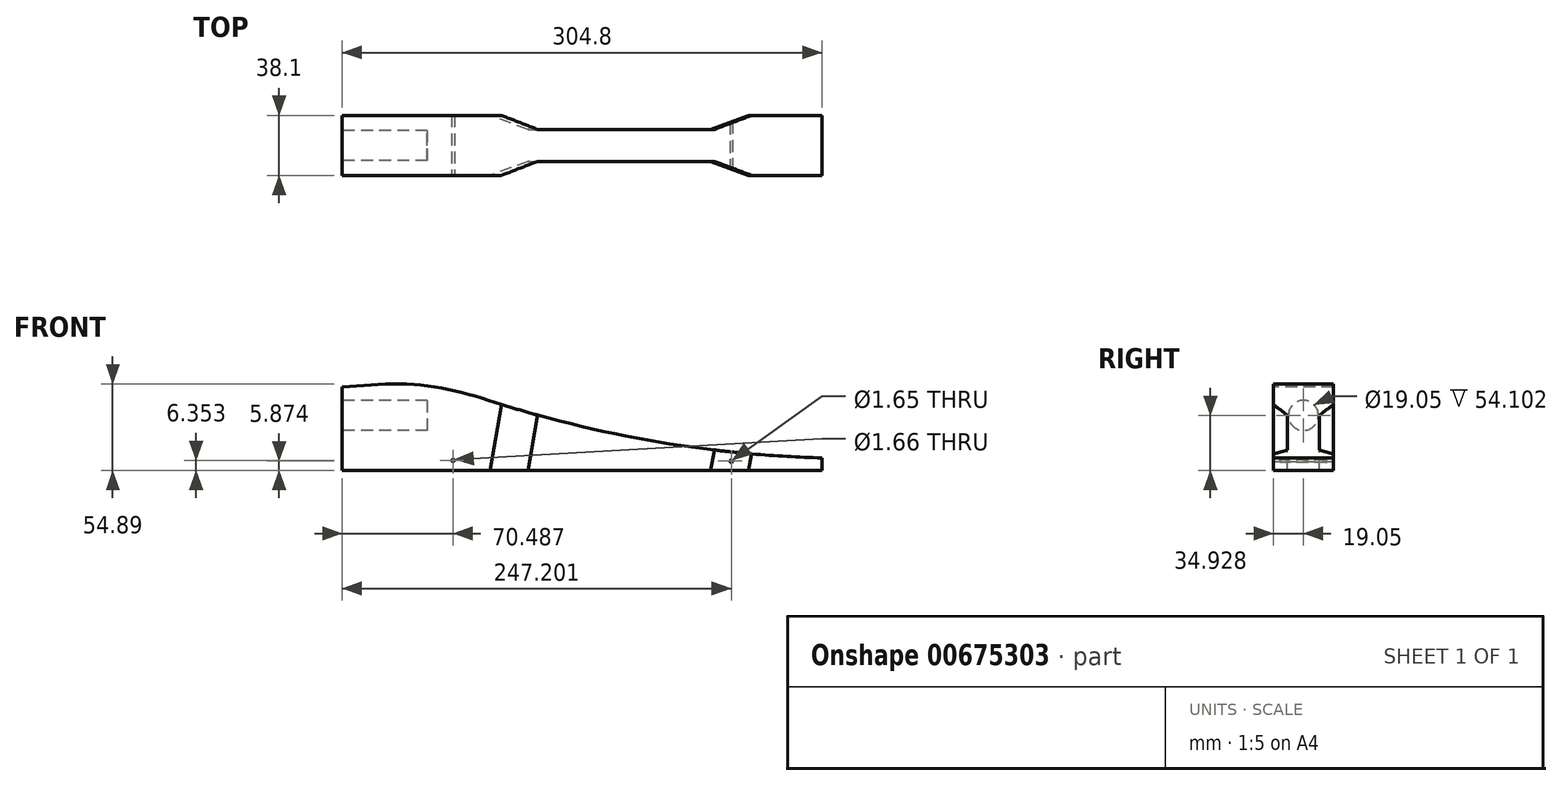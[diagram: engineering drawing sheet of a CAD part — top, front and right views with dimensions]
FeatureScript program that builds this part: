
annotation { "Feature Type Name" : "Feature", "Feature Type Description" : "" }
export const myFeature = defineFeature(function(context is Context, id is Id, definition is map)
    precondition{}
    {
        {
            var Q0;
            Q0=qCreatedBy(makeId("Front.planeOp"),FACE);
            var sketch = newSketch(context, id + "F0", { "sketchPlane" : qUnion([Q0])});
            skLineSegment(sketch, "E0.bottom", {"start": v(-104.5, 9.8) * mm, "end": v(200.3, 9.8) * mm});
            skLineSegment(sketch, "E0.top", {"start": v(-104.5, -60.06) * mm, "end": v(200.3, -60.06) * mm});
            skLineSegment(sketch, "E0.left", {"start": v(-104.5, 9.8) * mm, "end": v(-104.5, -60.06) * mm});
            skLineSegment(sketch, "E0.right", {"start": v(200.3, 9.8) * mm, "end": v(200.3, -60.06) * mm});
            skSolve(sketch);
        }
        {
            var Q0;
            Q0=makeQuery(id+"F0.imprint","IMPRINT",FACE,{"disambiguationData":[TD([[makeQuery(id+"F0.imprint","IMPRINT",EDGE,{"derivedFrom":sQuery(id+"F0.wireOp",EDGE,"E0.bottom")}),-1.0]])]});
            extrude(context, id + "F1", {"entities" : qUnion([Q0]), "oppositeDirection" : true, "depth" : 38.1 * mm, "offsetDistance" : 25.4 * mm});
        }
        {
            var Q0;
            Q0=makeQuery(id+"F1.opExtrude","CAP_FACE",FACE,{"disambiguationData":[OSD([sQuery(id+"F0.wireOp",EDGE,"E0.bottom"),sQuery(id+"F0.wireOp",EDGE,"E0.top"),sQuery(id+"F0.wireOp",EDGE,"E0.left"),sQuery(id+"F0.wireOp",EDGE,"E0.right")])],"isStart":true});
            var sketch = newSketch(context, id + "F2", { "sketchPlane" : qUnion([Q0])});
            skLineSegment(sketch, "E1", {"start": v(-104.5, 9.8) * mm, "end": v(200.3, -44.18) * mm});
            skLineSegment(sketch, "E2", {"start": v(200.3, -44.18) * mm, "end": v(200.3, -60.06) * mm});
            skLineSegment(sketch, "E3", {"start": v(200.3, -60.06) * mm, "end": v(-104.5, -60.06) * mm});
            skLineSegment(sketch, "E4", {"start": v(-104.5, -60.06) * mm, "end": v(-104.5, 9.8) * mm});
            skSolve(sketch);
        }
        {
            var Q0;
            {var subQ0=sQuery(id+"F2.wireOp",EDGE,"E1");Q0=makeQuery(id+"F2.imprint","IMPRINT",FACE,{"disambiguationData":[TD([[makeQuery(id+"F2.imprint","IMPRINT",EDGE,{"derivedFrom":subQ0}),1.0]])]});}
            extrude(context, id + "F3", {"entities" : qUnion([Q0]), "operationType" : NewBodyOperationType.REMOVE, "oppositeDirection" : true, "depth" : 50.8 * mm, "offsetDistance" : 25.4 * mm});
        }
        {
            var Q0;
            Q0=makeQuery(id+"F1.opExtrude","SWEPT_FACE",FACE,{"disambiguationData":[OSD([sQuery(id+"F0.wireOp",EDGE,"E0.left")])]});
            var sketch = newSketch(context, id + "F4", { "sketchPlane" : qUnion([Q0])});
            skCircle(sketch, "E5", {"center": v(-19.05, -25.13) * mm, "radius": 9.53 * mm});
            skPoint(sketch, "E6.orphan", {"position": v(-19.05, 9.8) * mm});
            skPoint(sketch, "E7.start.orphan", {"position": v(-38.1, -25.13) * mm});
            skPoint(sketch, "E8.trimOffspring.end.orphan", {"position": v(0, -25.13) * mm});
            skPoint(sketch, "E9.end.orphan", {"position": v(-19.05, -60.06) * mm});
            skSolve(sketch);
        }
        {
            var Q0;
            Q0=makeQuery(id+"F4.imprint","IMPRINT",FACE,{"disambiguationData":[TD([[makeQuery(id+"F4.imprint","IMPRINT",EDGE,{"derivedFrom":sQuery(id+"F4.wireOp",EDGE,"E5")}),1.0]])]});
            extrude(context, id + "F5", {"entities" : qUnion([Q0]), "operationType" : NewBodyOperationType.REMOVE, "oppositeDirection" : true, "depth" : 54.1 * mm, "offsetDistance" : 25.4 * mm});
        }
        {
            var Q0;
            Q0=makeQuery(id+"F3.boolean.opBoolean","COPY",FACE,{"derivedFrom":makeQuery(id+"F3.opExtrude","SWEPT_FACE",FACE,{"disambiguationData":[OSD([sQuery(id+"F2.wireOp",EDGE,"E1")])]})});
            var sketch = newSketch(context, id + "F6", { "sketchPlane" : qUnion([Q0])});
            skLineSegment(sketch, "E10", {"start": v(0, 0) * mm, "end": v(23.78, 8.92) * mm});
            skLineSegment(sketch, "E11", {"start": v(23.78, 8.92) * mm, "end": v(138.08, 8.92) * mm});
            skLineSegment(sketch, "E12", {"start": v(138.08, 8.92) * mm, "end": v(161.86, 0) * mm});
            skLineSegment(sketch, "E13", {"start": v(161.86, 0) * mm, "end": v(0, 0) * mm});
            skPoint(sketch, "E14.MirrorCS.end.orphan", {"position": v(109.86, 84.13) * mm});
            skPoint(sketch, "E14.MirrorCS.start.orphan", {"position": v(23.78, 8.92) * mm});
            skLineSegment(sketch, "E15", {"start": v(0, 38.1) * mm, "end": v(23.78, 29.18) * mm});
            skLineSegment(sketch, "E16", {"start": v(23.78, 29.18) * mm, "end": v(138.08, 29.18) * mm});
            skLineSegment(sketch, "E17", {"start": v(138.08, 29.18) * mm, "end": v(161.86, 38.1) * mm});
            skLineSegment(sketch, "E18", {"start": v(161.86, 38.1) * mm, "end": v(0, 38.1) * mm});
            skSolve(sketch);
        }
        {
            var Q0;
            Q0=makeQuery(id+"F6.imprint","IMPRINT",FACE,{"disambiguationData":[TD([[makeQuery(id+"F6.imprint","IMPRINT",EDGE,{"derivedFrom":sQuery(id+"F6.wireOp",EDGE,"E15")}),1.0]])]});
            var Q1;
            Q1=makeQuery(id+"F6.imprint","IMPRINT",FACE,{"disambiguationData":[TD([[makeQuery(id+"F6.imprint","IMPRINT",EDGE,{"derivedFrom":sQuery(id+"F6.wireOp",EDGE,"E10")}),-1.0]])]});
            extrude(context, id + "F7", {"entities" : qUnion([Q0, Q1]), "operationType" : NewBodyOperationType.REMOVE, "oppositeDirection" : true, "depth" : 127 * mm, "offsetDistance" : 25.4 * mm});
        }
        {
            var Q0;
            {var subQ0=sQuery(id+"F0.wireOp",EDGE,"E0.top");var subQ1=sQuery(id+"F0.wireOp",EDGE,"E0.left");Q0=makeQuery(id+"F7.boolean.opBoolean","SPLIT",FACE,{"disambiguationData":[TD([makeQuery(id+"F1.opExtrude","SWEPT_FACE",FACE,{"disambiguationData":[OSD([subQ1])]})])],"derivedFrom":makeQuery(id+"F1.opExtrude","CAP_FACE",FACE,{"disambiguationData":[OSD([sQuery(id+"F0.wireOp",EDGE,"E0.bottom"),subQ0,subQ1,sQuery(id+"F0.wireOp",EDGE,"E0.right")])],"isStart":true})});}
            var sketch = newSketch(context, id + "F8", { "sketchPlane" : qUnion([Q0])});
            skFitSpline(sketch, "E19", {"points": [v(-104.5, -7.03) * mm, v(-51.46, -6.13) * mm, v(-3.22, -18.16) * mm], "startDerivative": vector(105.99, 8.43) * mm, "endDerivative": vector(96.51, -30.92) * mm});
            skSolve(sketch);
        }
        {
            var Q0;
            Q0=qCreatedBy(makeId("Front.planeOp"),FACE);
            var sketch = newSketch(context, id + "F9", { "sketchPlane" : qUnion([Q0])});
            skLineSegment(sketch, "E20.0.0", {"start": v(13.52, -60.06) * mm, "end": v(21.92, -12.6) * mm});
            skLineSegment(sketch, "E20.0.1", {"start": v(21.92, -12.6) * mm, "end": v(-1.5, -8.45) * mm});
            skLineSegment(sketch, "E20.0.2", {"start": v(-1.5, -8.45) * mm, "end": v(-3.22, -18.16) * mm});
            skLineSegment(sketch, "E20.0.3", {"start": v(-3.22, -18.16) * mm, "end": v(-10.64, -60.06) * mm});
            skLineSegment(sketch, "E20.0.4", {"start": v(-10.64, -60.06) * mm, "end": v(13.52, -60.06) * mm});
            skLineSegment(sketch, "E21.0.0", {"start": v(129.6, -60.06) * mm, "end": v(134.47, -32.52) * mm});
            skLineSegment(sketch, "E21.0.1", {"start": v(134.47, -32.52) * mm, "end": v(21.92, -12.6) * mm});
            skLineSegment(sketch, "E21.0.2", {"start": v(21.92, -12.6) * mm, "end": v(13.52, -60.06) * mm});
            skLineSegment(sketch, "E21.0.3", {"start": v(13.52, -60.06) * mm, "end": v(129.6, -60.06) * mm});
            skLineSegment(sketch, "E22.0.0", {"start": v(153.74, -60.06) * mm, "end": v(157.89, -36.67) * mm});
            skLineSegment(sketch, "E22.0.1", {"start": v(157.89, -36.67) * mm, "end": v(134.47, -32.52) * mm});
            skLineSegment(sketch, "E22.0.2", {"start": v(134.47, -32.52) * mm, "end": v(129.6, -60.06) * mm});
            skLineSegment(sketch, "E22.0.3", {"start": v(129.6, -60.06) * mm, "end": v(153.74, -60.06) * mm});
            skLineSegment(sketch, "E23.0.0", {"start": v(157.89, -36.67) * mm, "end": v(153.74, -60.06) * mm});
            skLineSegment(sketch, "E23.0.1", {"start": v(153.74, -60.06) * mm, "end": v(200.3, -60.06) * mm});
            skLineSegment(sketch, "E23.0.2", {"start": v(200.3, -60.06) * mm, "end": v(200.3, -44.18) * mm});
            skLineSegment(sketch, "E23.0.3", {"start": v(200.3, -44.18) * mm, "end": v(157.89, -36.67) * mm});
            skArc(sketch, "E24", {"start": v(-3.22, -18.16) * mm, "mid": v(97.38, -42.15) * mm, "end": v(200.3, -52.12) * mm});
            skSolve(sketch);
        }
        {
            var Q0;
            {var subQ0=sQuery(id+"F8.wireOp",EDGE,"E19");Q0=makeQuery(id+"F8.imprint","IMPRINT",FACE,{"disambiguationData":[TD([[makeQuery(id+"F8.imprint","IMPRINT",EDGE,{"derivedFrom":subQ0}),1.0]])]});}
            var Q1;
            {var subQ0=sQuery(id+"F9.wireOp",EDGE,"E20.0.1");Q1=makeQuery(id+"F9.imprint","IMPRINT",FACE,{"disambiguationData":[TD([[makeQuery(id+"F9.imprint","IMPRINT",EDGE,{"derivedFrom":subQ0}),1.0]])]});}
            var Q2;
            {var subQ0=sQuery(id+"F9.wireOp",EDGE,"E23.0.3");Q2=makeQuery(id+"F9.imprint","IMPRINT",FACE,{"disambiguationData":[TD([[makeQuery(id+"F9.imprint","IMPRINT",EDGE,{"derivedFrom":subQ0}),1.0]])]});}
            var Q3;
            {var subQ0=sQuery(id+"F9.wireOp",EDGE,"E22.0.1");Q3=makeQuery(id+"F9.imprint","IMPRINT",FACE,{"disambiguationData":[TD([[makeQuery(id+"F9.imprint","IMPRINT",EDGE,{"derivedFrom":subQ0}),1.0]])]});}
            var Q4;
            {var subQ0=sQuery(id+"F9.wireOp",EDGE,"E21.0.1");Q4=makeQuery(id+"F9.imprint","IMPRINT",FACE,{"disambiguationData":[TD([[makeQuery(id+"F9.imprint","IMPRINT",EDGE,{"derivedFrom":subQ0}),1.0]])]});}
            extrude(context, id + "F10", {"entities" : qUnion([Q0, Q1, Q2, Q3, Q4]), "operationType" : NewBodyOperationType.REMOVE, "oppositeDirection" : true, "depth" : 76.2 * mm, "offsetDistance" : 25.4 * mm});
        }
        {
            var Q0;
            Q0=qCreatedBy(makeId("Front.planeOp"),FACE);
            var sketch = newSketch(context, id + "F11", { "sketchPlane" : qUnion([Q0])});
            skPoint(sketch, "E25.0", {"position": v(154.67, -54.8) * mm});
            skPoint(sketch, "E26.0", {"position": v(130.74, -53.57) * mm});
            skPoint(sketch, "E27.0", {"position": v(143.74, -48.4) * mm});
            skPoint(sketch, "E28.0", {"position": v(141.67, -60.06) * mm});
            skCircle(sketch, "E29", {"center": v(142.71, -54.19) * mm, "radius": 0.83 * mm});
            skSolve(sketch);
        }
        {
            var Q0;
            Q0 = qSketchRegion(id + "F11", true);
            extrude(context, id + "F12", {"entities" : qUnion([Q0]), "operationType" : NewBodyOperationType.REMOVE, "oppositeDirection" : true, "depth" : 76.2 * mm, "offsetDistance" : 25.4 * mm});
        }
        {
            var Q0;
            Q0=qCreatedBy(makeId("Front.planeOp"),FACE);
            var sketch = newSketch(context, id + "F13", { "sketchPlane" : qUnion([Q0])});
            skPoint(sketch, "E30.0", {"position": v(-53.1, -5.95) * mm});
            skFitSpline(sketch, "E31.0", {"points": [v(-104.5, -7.03) * mm, v(-86.54, -5.6) * mm, v(-51.21, -2.79) * mm, v(-19.04, -13.1) * mm, v(-3.22, -18.16) * mm]});
            skLineSegment(sketch, "E32.0", {"start": v(-10.64, -60.06) * mm, "end": v(-3.22, -18.16) * mm});
            skPoint(sketch, "E33.0", {"position": v(-6.93, -39.11) * mm});
            skLineSegment(sketch, "E34.0", {"start": v(-104.5, -60.06) * mm, "end": v(-10.64, -60.06) * mm});
            skPoint(sketch, "E34.1", {"position": v(-57.56, -60.06) * mm});
            skLineSegment(sketch, "E35.0", {"start": v(-104.5, -7.03) * mm, "end": v(-104.5, -60.06) * mm});
            skPoint(sketch, "E35.1", {"position": v(-104.5, -33.54) * mm});
            skCircle(sketch, "E36", {"center": v(-34, -53.7) * mm, "radius": 0.83 * mm});
            skPoint(sketch, "E37.start.orphan", {"position": v(-9.51, -53.7) * mm});
            skPoint(sketch, "E38.start.orphan", {"position": v(-34, -60.06) * mm});
            skSolve(sketch);
        }
        {
            var Q0;
            Q0=makeQuery(id+"F13.imprint","IMPRINT",FACE,{"disambiguationData":[TD([[makeQuery(id+"F13.imprint","IMPRINT",EDGE,{"derivedFrom":sQuery(id+"F13.wireOp",EDGE,"E36")}),1.0]])]});
            extrude(context, id + "F14", {"entities" : qUnion([Q0]), "operationType" : NewBodyOperationType.REMOVE, "oppositeDirection" : true, "depth" : 76.2 * mm, "offsetDistance" : 25.4 * mm});
        }
    });
